# Revit family: NLRS_57_DUA_UN_Round_Attenuator_LT_AGR_V_Solid_Air
name_source: partatom
category: Duct Accessories
revit_build: Autodesk Revit 2017 (Build: 20190508_0315(x64)
units: mm (PartAtom-declared; Revit-internal decimal feet)

## family parameters
Always vertical = Yes
Cut with Voids When Loaded = No
Part Type = Breaks Into
Round Connector Dimension = Use Diameter
Shared = No
Work Plane-Based = No

## types (10) — shared parameters
Assembly Code = 57.70
Code = AGR_Article_Codes
Description = Ronde geluiddemper
Manufacturer = Solid Air Climate Solutions
Model = VAV regelaar - Rond
NLRS_C_content_datum_uitgifte = 14-01-2020
NLRS_C_content_provider = Solid Air Climate Systems
NLRS_C_content_versie = Versie 1.7
NLRS_C_description = Ronde geluiddemper
NLRS_C_niveau ontwikkeling = LOD400
SACS_AX_Prefix = 935
SACS_Dummy = 1
Type Comments = Check flow direction!
data = AGR_Article_Data

## per-type parameters (varying)
| type | External_Diameter | Internal_Diameter | SACS_Diameter |
| 200 | 198 mm | 196 mm | 200 mm  [stored 0.656168 ft] |
| 250 | 248 mm | 246 mm | 250 mm  [stored 0.82021 ft] |
| 315 | 313 mm  [stored 1.0269 ft] | 311 mm | 315 mm  [stored 1.03346 ft] |
| 160 | 158 mm | 156 mm | 160 mm  [stored 0.524934 ft] |
| 125 | 123 mm  [stored 0.403543 ft] | 121 mm  [stored 0.396982 ft] | 125 mm  [stored 0.410105 ft] |
| 100 | 98 mm  [stored 0.321522 ft] | 96 mm  [stored 0.314961 ft] | 100 mm  [stored 0.328084 ft] |
| 400 | 398 mm  [stored 1.30577 ft] | 396 mm  [stored 1.29921 ft] | 400 mm  [stored 1.31234 ft] |
| 080 | 78 mm  [stored 0.255906 ft] | 76 mm  [stored 0.249344 ft] | 80 mm  [stored 0.262467 ft] |
| 500 | 498 mm  [stored 1.63386 ft] | 496 mm  [stored 1.6273 ft] | 500 mm  [stored 1.64042 ft] |
| 630 | 628 mm  [stored 2.06037 ft] | 626 mm | 630 mm  [stored 2.06693 ft] |

note: [stored X ft] marks values corroborated as IEEE doubles in the binary element streams (Revit-internal decimal feet)

## geometry (parser evidence)
native form markers: Sweep x4
no freeform markers — native parametric forms only
